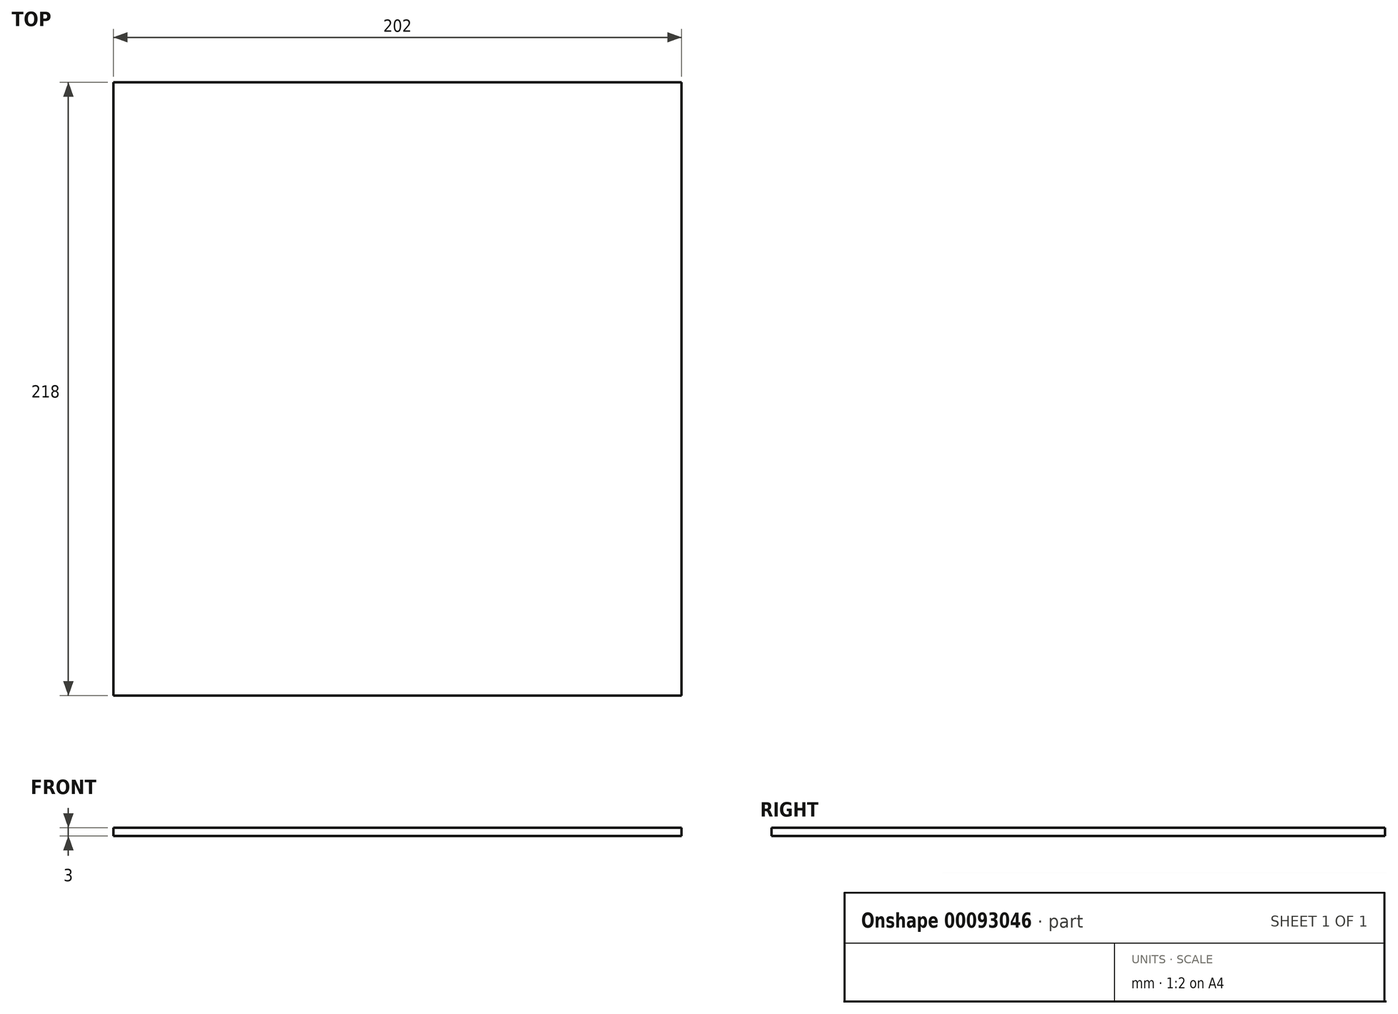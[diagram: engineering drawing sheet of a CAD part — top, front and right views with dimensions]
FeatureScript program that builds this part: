
annotation { "Feature Type Name" : "Feature", "Feature Type Description" : "" }
export const myFeature = defineFeature(function(context is Context, id is Id, definition is map)
    precondition{}
    {
        {
            var Q0;
            Q0=qCreatedBy(makeId("Top.planeOp"),FACE);
            var sketch = newSketch(context, id + "F0", { "sketchPlane" : qUnion([Q0])});
            skLineSegment(sketch, "E0.bottom", {"start": v(4, 0) * mm, "end": v(206, 0) * mm});
            skLineSegment(sketch, "E0.top", {"start": v(4, 218) * mm, "end": v(206, 218) * mm});
            skLineSegment(sketch, "E0.left", {"start": v(4, 0) * mm, "end": v(4, 218) * mm});
            skLineSegment(sketch, "E0.right", {"start": v(206, 0) * mm, "end": v(206, 218) * mm});
            skSolve(sketch);
        }
        {
            var Q0;
            Q0 = qSketchRegion(id + "F0", true);
            extrude(context, id + "F1", {"entities" : qUnion([Q0]), "oppositeDirection" : true, "depth" : 3 * mm});
        }
    });
